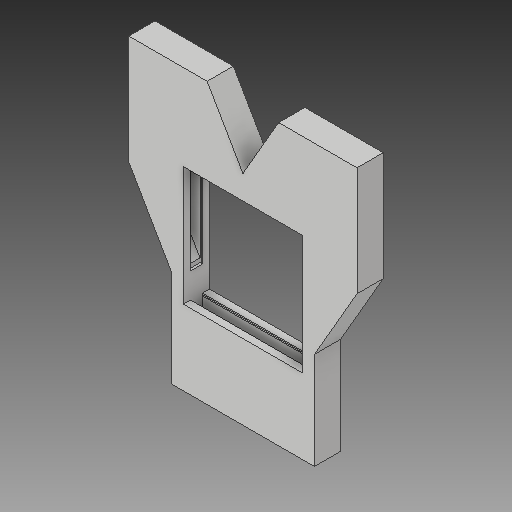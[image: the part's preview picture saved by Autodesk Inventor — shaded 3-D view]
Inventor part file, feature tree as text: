
AUTODESK INVENTOR PART (.ipt)
format: ipt  version: 2017 (Build 210142000, 142)  size: 181,760 bytes
history: native  units: in
note: dims shown in document units (in); Inventor stores cm internally (conversion verified against a paired STEP export)
features: other x4, plane x1, sketch x1
ambient origin geometry x8: Origin, YZ Plane, XZ Plane, XY Plane, X Axis, Y Axis, Z Axis, Center Point
bodies: Solid1 (feature_tree)
feature tree (6):
  other  "end door frame (100).ipt"
  plane  "Work Plane1"
  sketch  "Sketch1"  dims[d0=0.0354in d1=4.5in]
  other  "mate for doors"
  other  "rame of door::end door frame (100).ipt"
  other  "TaggingFeature1"
